# Revit family: Секция трехрядного водяного нагревателя AIRNED-M N1.3
name_source: partatom
category: Оборудование
revit_build: Autodesk Revit 2017 (Build: 20160225_1515(x64)
units: mm (PartAtom-declared; Revit-internal decimal feet)

## family parameters
Всегда вертикально = Да
На основе рабочей плоскости = Нет
Общий = Нет
При загрузке вырезать с полостями = Нет
Размер круглого соединителя = Использовать диаметр
Тип детали = Нормальный
Точка расчета площади = Нет

## types (10) — shared parameters
h = 130 мм
Д = 575 мм
Д1 = 555 мм
Единица измерения = шт.
Завод изготовитель = NED
Ключевая пометка = Вентиляция
Наименование и тех.хар-ка = Секция трехрядного водяного нагревателя
Раздел = ОВ
высота ножек = 120 мм

## per-type parameters (varying)
| type | А | А1 | Б | Б1 | Высота | Г | Д патрубков | Заправочный объем, л | Материал | Размер В | Резьбовое соединение, дюймы | Середина | Ширина |
| AIRNED-M 6 N1.3 | 1100 мм | 1080 мм | 1100 мм | 1080 мм | 1025 мм | 85 мм | 30 мм | 8.2 м³ | Сталь серая | 722 мм | G1 1/2'' | 670 мм | 1025 мм |
| AIRNED-M 7 N1.3 | 1100 мм | 1080 мм | 1320 мм | 1300 мм | 1245 мм | 85 мм | 40 мм | 11.7 м³ | Сталь серая | 972 мм | G1 1/2'' | 780 мм | 1025 мм |
| AIRNED-M 8 N1.3 | 1320 мм | 1300 мм | 1320 мм | 1300 мм | 1245 мм | 85 мм | 51 мм | 15.8 м³ | Сталь серая | 985 мм | G2'' | 780 мм | 1245 мм |
| AIRNED-M 12 N1.3 | 1435 мм | 1415 мм | 1435 мм | 1415 мм | 1360 мм | 85 мм | 51 мм | 17.7 м³ | Сталь серая | 1152 мм | G2'' | 838 мм | 1360 мм |
| AIRNED-M 20 N1.3 | 1660 мм | 1640 мм | 1660 мм | 1640 мм | 1585 мм | 85 мм | 64 мм | 34.2 м³ | Сталь серая | 1355 мм | G2 1/2'' | 950 мм | 1585 мм |
| AIRNED-M 25 N1.3 | 2045 мм | 2025 мм | 2045 мм | 2025 мм | 1970 мм | 85 мм | 76 мм | 55.1 м³ | Сталь серая | 1740 мм | G3'' | 1143 мм | 1970 мм |
| AIRNED-M 30 N1.3 | 2485 мм | 2465 мм | 2045 мм | 2025 мм | 1970 мм | 100 мм | 76 мм | 65.7 м³ | Сталь серая | 1685 мм | G3'' | 1143 мм | 2410 мм |
| AIRNED-M 35 N1.3 | 2485 мм | 2465 мм | 2485 мм | 2465 мм | 2410 мм | 125 мм | 76 мм | 98 м³ | Сталь серая | 2100 мм | G3'' | 1363 мм | 2410 мм |
| AIRNED-M 40 N1.3 | 3320 мм | 3300 мм | 3320 мм | 3300 мм | 3245 мм | 100 мм | 102 мм | 138 м³ | Сталь серая | 1355 мм | G4'' | 1780 мм | 3245 мм |
| AIRNED-M 45 N1.3 | 3320 мм | 3300 мм | 4090 мм | 4070 мм | 4015 мм | 125 мм | 102 мм | 220 м³ | RAL 0000 Серый металл | 1740 мм | G4'' | 2165 мм | 3245 мм |

note: column(s) folded — value = type name in every type: Тип, марка, обозначение
